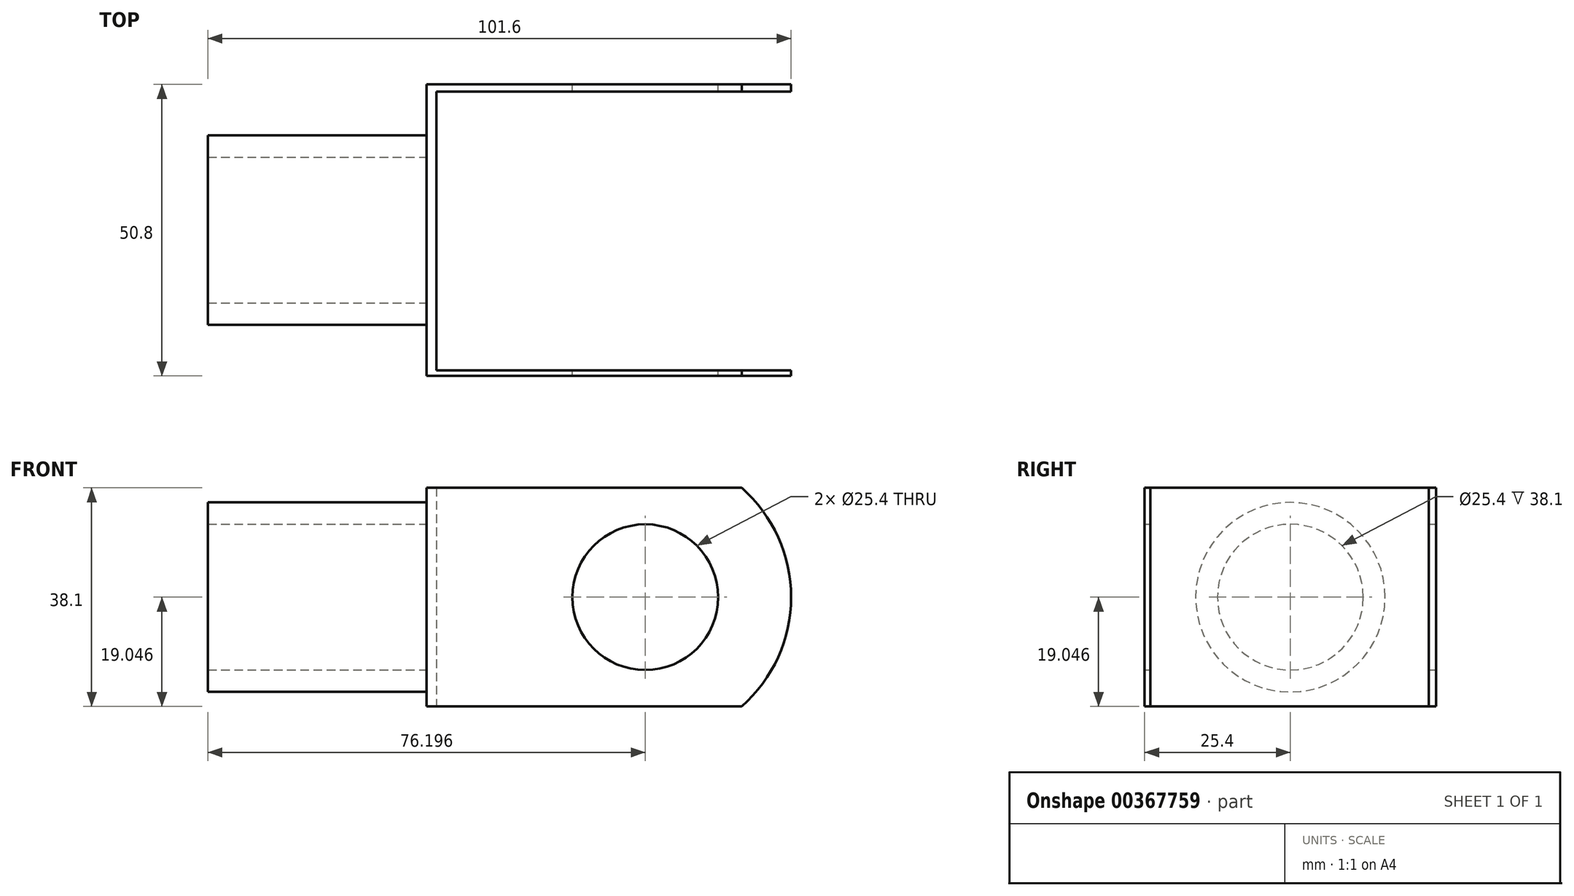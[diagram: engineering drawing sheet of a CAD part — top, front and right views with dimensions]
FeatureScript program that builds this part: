
annotation { "Feature Type Name" : "Feature", "Feature Type Description" : "" }
export const myFeature = defineFeature(function(context is Context, id is Id, definition is map)
    precondition{}
    {
        {
            var Q0;
            Q0=qCreatedBy(makeId("Front.planeOp"),FACE);
            var sketch = newSketch(context, id + "F0", { "sketchPlane" : qUnion([Q0])});
            skLineSegment(sketch, "E0.bottom", {"start": v(-25.5, -15.5) * mm, "end": v(12.6, -15.5) * mm});
            skLineSegment(sketch, "E0.top", {"start": v(-25.5, 35.3) * mm, "end": v(12.6, 35.3) * mm});
            skLineSegment(sketch, "E0.left", {"start": v(-25.5, -15.5) * mm, "end": v(-25.5, 35.3) * mm});
            skArc(sketch, "E1", {"start": v(12.6, -15.5) * mm, "mid": v(38, 9.9) * mm, "end": v(12.6, 35.3) * mm});
            skCircle(sketch, "E2", {"center": v(12.6, 9.9) * mm, "radius": 12.7 * mm});
            skSolve(sketch);
        }
        {
            var Q0;
            Q0=makeQuery(id+"F0.imprint","IMPRINT",FACE,{"disambiguationData":[TD([[makeQuery(id+"F0.imprint","IMPRINT",EDGE,{"derivedFrom":sQuery(id+"F0.wireOp",EDGE,"E0.bottom")}),1.0]])]});
            extrude(context, id + "F1", {"entities" : qUnion([Q0]), "depth" : 50.8 * mm});
        }
        {
            var Q0;
            Q0=qCreatedBy(makeId("Right.planeOp"),FACE);
            var sketch = newSketch(context, id + "F2", { "sketchPlane" : qUnion([Q0])});
            skLineSegment(sketch, "E3.bottom", {"start": v(-49.8, 37.04) * mm, "end": v(-1.27, 37.04) * mm});
            skLineSegment(sketch, "E3.top", {"start": v(-49.8, -17.78) * mm, "end": v(-1.27, -17.78) * mm});
            skLineSegment(sketch, "E3.left", {"start": v(-49.8, 37.04) * mm, "end": v(-49.8, -17.78) * mm});
            skLineSegment(sketch, "E3.right", {"start": v(-1.27, 37.04) * mm, "end": v(-1.27, -17.78) * mm});
            skSolve(sketch);
        }
        {
            var Q0;
            Q0 = qSketchRegion(id + "F2", true);
            extrude(context, id + "F3", {"entities" : qUnion([Q0]), "operationType" : NewBodyOperationType.REMOVE, "endBound" : BoundingType.SYMMETRIC, "oppositeDirection" : true, "depth" : 47.62 * mm});
        }
        {
            var Q0;
            Q0=makeQuery(id+"F3.boolean.opBoolean","COPY",FACE,{"derivedFrom":makeQuery(id+"F3.opExtrude","CAP_FACE",FACE,{"disambiguationData":[OSD([sQuery(id+"F2.wireOp",EDGE,"E3.bottom"),sQuery(id+"F2.wireOp",EDGE,"E3.top"),sQuery(id+"F2.wireOp",EDGE,"E3.left"),sQuery(id+"F2.wireOp",EDGE,"E3.right")])],"isStart":false})});
            var sketch = newSketch(context, id + "F4", { "sketchPlane" : qUnion([Q0])});
            skLineSegment(sketch, "E4.bottom", {"start": v(-1.27, 35.3) * mm, "end": v(-49.8, 35.3) * mm});
            skLineSegment(sketch, "E4.top", {"start": v(-1.27, -15.5) * mm, "end": v(-49.8, -15.5) * mm});
            skLineSegment(sketch, "E4.left", {"start": v(-1.27, 35.3) * mm, "end": v(-1.27, -15.5) * mm});
            skLineSegment(sketch, "E4.right", {"start": v(-49.8, 35.3) * mm, "end": v(-49.8, -15.5) * mm});
            skSolve(sketch);
        }
        {
            var Q0;
            Q0 = qSketchRegion(id + "F4", true);
            extrude(context, id + "F5", {"entities" : qUnion([Q0]), "operationType" : NewBodyOperationType.REMOVE, "depth" : 76.2 * mm});
        }
        {
            var Q0;
            Q0=makeQuery(id+"F1.opExtrude","SWEPT_FACE",FACE,{"disambiguationData":[OSD([sQuery(id+"F0.wireOp",EDGE,"E0.left")])]});
            var sketch = newSketch(context, id + "F6", { "sketchPlane" : qUnion([Q0])});
            skCircle(sketch, "E5", {"center": v(25.4, 9.9) * mm, "radius": 16.51 * mm});
            skPoint(sketch, "E5.centerSnap0", {"position": v(25.4, 35.3) * mm});
            skPoint(sketch, "E5.centerSnap1", {"position": v(0, 9.9) * mm});
            skCircle(sketch, "E6", {"center": v(25.4, 9.9) * mm, "radius": 12.7 * mm});
            skSolve(sketch);
        }
        {
            var Q0;
            Q0 = qSketchRegion(id + "F6", true);
            extrude(context, id + "F7", {"entities" : qUnion([Q0]), "operationType" : NewBodyOperationType.ADD, "depth" : 38.1 * mm});
        }
        {
            var Q0;
            {var subQ3=sQuery(id+"F0.wireOp",EDGE,"E0.left");var subQ4=sQuery(id+"F0.wireOp",EDGE,"E0.bottom");Q0=makeQuery(id+"F7.boolean.opBoolean","SPLIT",FACE,{"disambiguationData":[TD([makeQuery(id+"F1.opExtrude","SWEPT_FACE",FACE,{"disambiguationData":[OSD([subQ4])]})])],"derivedFrom":makeQuery(id+"F1.opExtrude","SWEPT_FACE",FACE,{"disambiguationData":[OSD([subQ3])]})});}
            var sketch = newSketch(context, id + "F8", { "sketchPlane" : qUnion([Q0])});
            skLineSegment(sketch, "E7", {"start": v(0, 35.3) * mm, "end": v(0, 28.95) * mm});
            skLineSegment(sketch, "E8", {"start": v(0, 28.95) * mm, "end": v(50.8, 28.95) * mm});
            skLineSegment(sketch, "E9", {"start": v(50.8, 28.95) * mm, "end": v(50.8, 35.3) * mm});
            skLineSegment(sketch, "E10", {"start": v(50.8, 35.3) * mm, "end": v(0, 35.3) * mm});
            skLineSegment(sketch, "E11", {"start": v(0, -15.5) * mm, "end": v(50.8, -15.5) * mm});
            skLineSegment(sketch, "E12", {"start": v(50.8, -15.5) * mm, "end": v(50.8, -9.15) * mm});
            skLineSegment(sketch, "E13", {"start": v(50.8, -9.15) * mm, "end": v(0, -9.15) * mm});
            skLineSegment(sketch, "E14", {"start": v(0, -9.15) * mm, "end": v(0, -15.5) * mm});
            skSolve(sketch);
        }
        {
            var Q0;
            Q0 = qSketchRegion(id + "F8", true);
            extrude(context, id + "F9", {"entities" : qUnion([Q0]), "operationType" : NewBodyOperationType.REMOVE, "oppositeDirection" : true, "depth" : 101.6 * mm});
        }
    });
